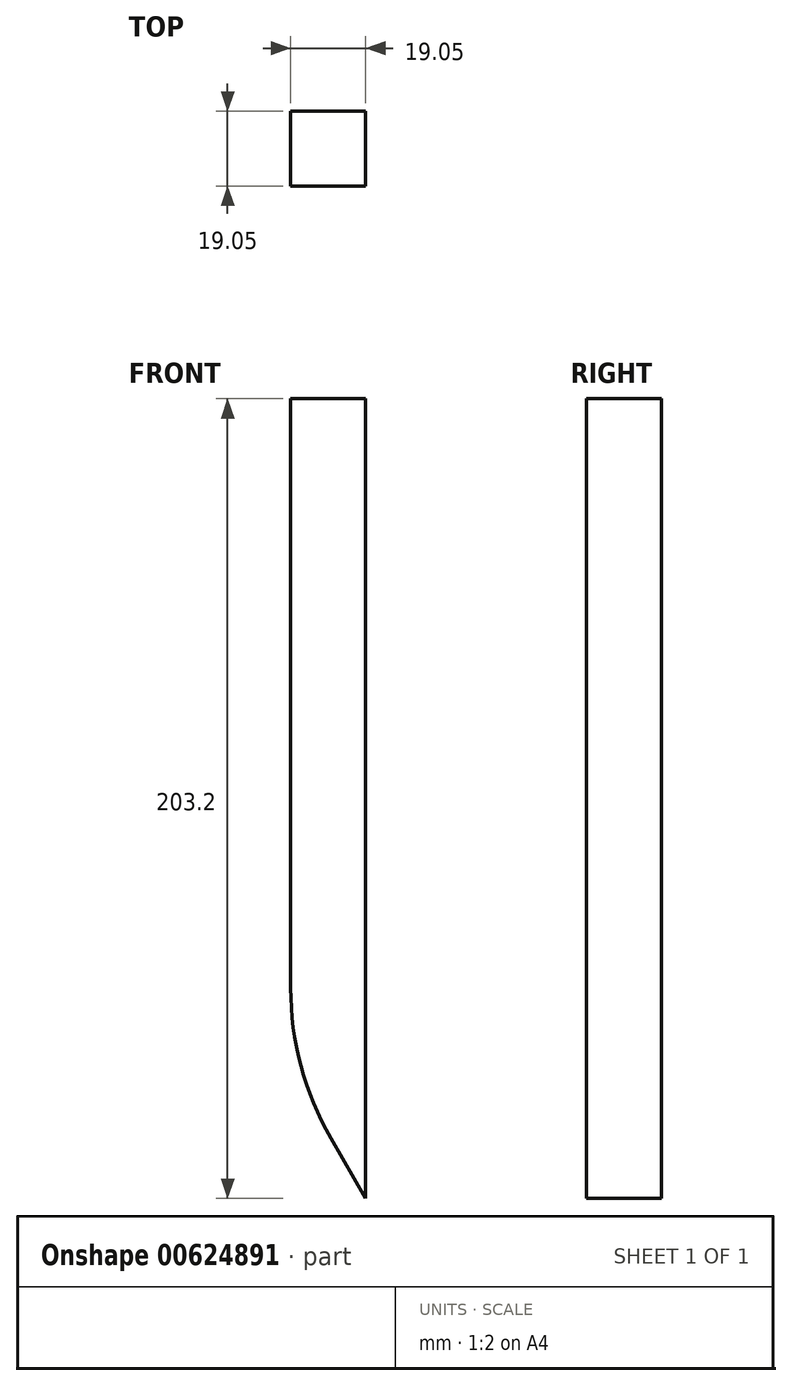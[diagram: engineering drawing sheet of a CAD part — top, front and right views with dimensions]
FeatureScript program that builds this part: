
annotation { "Feature Type Name" : "Feature", "Feature Type Description" : "" }
export const myFeature = defineFeature(function(context is Context, id is Id, definition is map)
    precondition{}
    {
        {
            var Q0;
            Q0=qCreatedBy(makeId("Front.planeOp"),FACE);
            var sketch = newSketch(context, id + "F0", { "sketchPlane" : qUnion([Q0])});
            skLineSegment(sketch, "E0", {"start": v(0, 0) * mm, "end": v(-8.84, 15.31) * mm});
            skLineSegment(sketch, "E1", {"start": v(-19.05, 53.41) * mm, "end": v(-19.05, 203.2) * mm});
            skLineSegment(sketch, "E2", {"start": v(-33.93, 188.32) * mm, "end": v(-34.38, 188.77) * mm});
            skLineSegment(sketch, "E3", {"start": v(-19.05, 203.2) * mm, "end": v(0, 203.2) * mm});
            skLineSegment(sketch, "E4", {"start": v(0, 203.2) * mm, "end": v(0, 0) * mm});
            skPoint(sketch, "E5.visualSharp", {"position": v(-19.05, 33) * mm});
            skArc(sketch, "E5.filletArc", {"start": v(-19.05, 53.41) * mm, "mid": v(-16.45, 33.7) * mm, "end": v(-8.84, 15.31) * mm});
            skPoint(sketch, "E6.visualSharp", {"position": v(-19.05, 173.44) * mm});
            skSolve(sketch);
        }
        {
            var Q0;
            Q0=makeQuery(id+"F0.imprint","IMPRINT",FACE,{"disambiguationData":[TD([[makeQuery(id+"F0.imprint","IMPRINT",EDGE,{"derivedFrom":sQuery(id+"F0.wireOp",EDGE,"E0")}),-1.0]])]});
            extrude(context, id + "F1", {"entities" : qUnion([Q0]), "depth" : 19.05 * mm, "offsetDistance" : 25.4 * mm});
        }
    });
